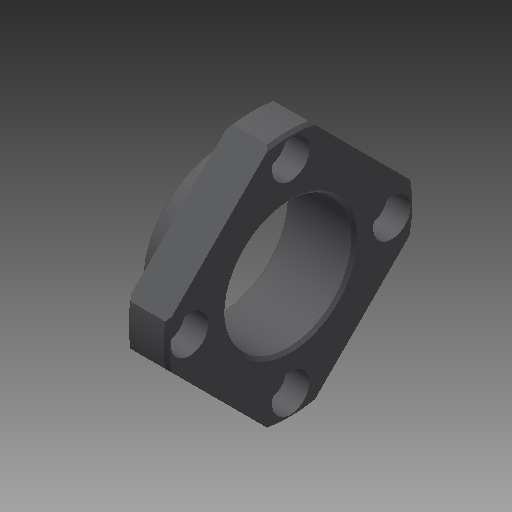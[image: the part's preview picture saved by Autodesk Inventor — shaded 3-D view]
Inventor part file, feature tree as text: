
AUTODESK INVENTOR PART (.ipt)
format: ipt  version: 2018 (Build 220112000, 112)  size: 178,688 bytes
history: native  units: mm
features: other x14, sketch x3, revolve x1, extrude x1, hole x1, pattern_linear x1
ambient origin geometry x8: Origin, YZ Plane, XZ Plane, XY Plane, X Axis, Y Axis, Z Axis, Center Point
bodies: Solid1 (feature_tree)
feature tree (21):
  revolve  "Revolution1"  [1 undecoded]
  extrude  "Extrusion1"  Depth=7.0mm
  hole  "Hole1"  [1 undecoded]
  pattern_linear  "Rectangular Pattern1"  [2 undecoded]
  other  "ff_1_XY"
  other  "ff_1_YZ"
  other  "ff_1_ZX"
  other  "ff_1_X"
  other  "ff_1_Y"
  other  "ff_1_Z"
  other  "ff_1_Center"
  other  "ff_2x_XY"
  other  "ff_2x_YZ"
  other  "ff_2x_ZX"
  other  "ff_2x_X"
  other  "ff_2x_Y"
  other  "ff_2x_Z"
  other  "ff_2x_Center"
  sketch  "Sketch_1"  dims[d0=360.0deg d1=7.0mm d2=0.0mm]
  sketch  "Sketch_2"  dims[d3=3.4mm d4=6.0mm d5=6.5mm d6=4.0mm d7=90.0deg d8=7.0mm d9=0.0mm d10=20.0mm d12=24.748737mm d13=20.0mm d15=24.748737mm]
  sketch  "Sketch3"  dims[d16=0.0mm]
note: 4 required parameter values undecoded (feature->parameter linkage not recoverable at this tier; creation-order binding heuristic only, values carry confidence <= 0.55)